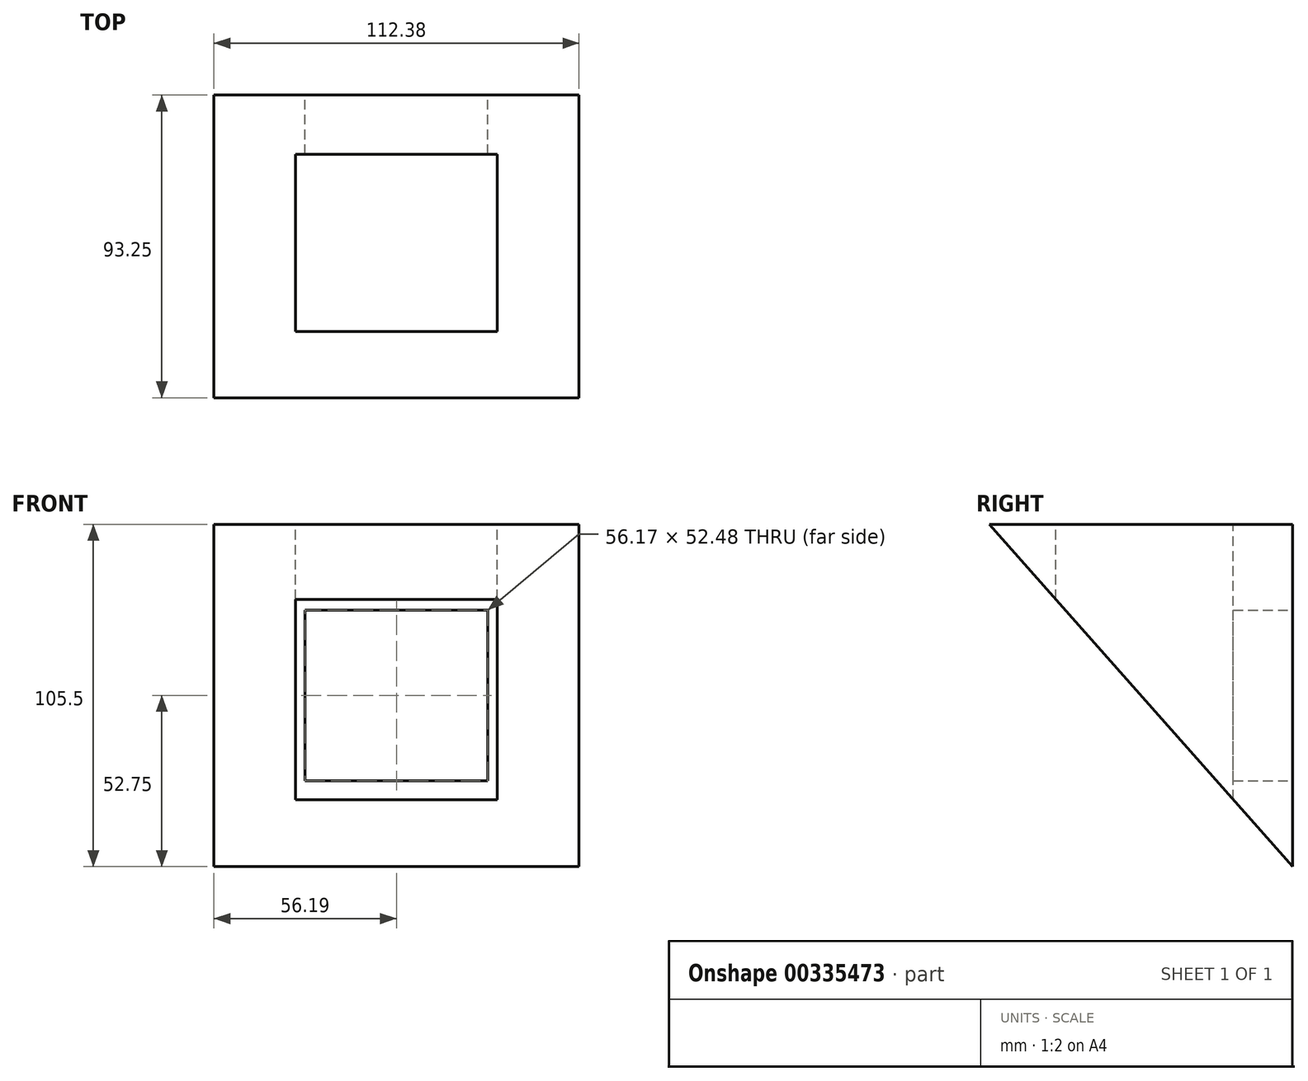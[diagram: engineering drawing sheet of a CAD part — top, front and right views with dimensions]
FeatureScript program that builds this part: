
annotation { "Feature Type Name" : "Feature", "Feature Type Description" : "" }
export const myFeature = defineFeature(function(context is Context, id is Id, definition is map)
    precondition{}
    {
        {
            var Q0;
            Q0=qCreatedBy(makeId("Front.planeOp"),FACE);
            var sketch = newSketch(context, id + "F0", { "sketchPlane" : qUnion([Q0])});
            skLineSegment(sketch, "E0.bottom", {"start": v(28.09, 26.24) * mm, "end": v(-28.09, 26.24) * mm});
            skLineSegment(sketch, "E0.top", {"start": v(28.09, -26.24) * mm, "end": v(-28.09, -26.24) * mm});
            skLineSegment(sketch, "E0.left", {"start": v(28.09, 26.24) * mm, "end": v(28.09, -26.24) * mm});
            skLineSegment(sketch, "E0.right", {"start": v(-28.09, 26.24) * mm, "end": v(-28.09, -26.24) * mm});
            skPoint(sketch, "E0.middle", {"position": v(0, 0) * mm});
            skLineSegment(sketch, "E1.bottom", {"start": v(-56.2, -52.75) * mm, "end": v(56.2, -52.75) * mm});
            skLineSegment(sketch, "E1.top", {"start": v(-56.2, 52.75) * mm, "end": v(56.2, 52.75) * mm});
            skLineSegment(sketch, "E1.left", {"start": v(-56.2, -52.75) * mm, "end": v(-56.2, 52.75) * mm});
            skLineSegment(sketch, "E1.right", {"start": v(56.2, -52.75) * mm, "end": v(56.2, 52.75) * mm});
            skSolve(sketch);
        }
        {
            var Q0;
            Q0=makeQuery(id+"F0.imprint","IMPRINT",FACE,{"disambiguationData":[TD([[makeQuery(id+"F0.imprint","IMPRINT",EDGE,{"derivedFrom":sQuery(id+"F0.wireOp",EDGE,"E0.bottom")}),-1.0]])]});
            extrude(context, id + "F1", {"entities" : qUnion([Q0]), "depth" : 93.25 * mm});
        }
        {
            var Q0;
            Q0=makeQuery(id+"F1.opExtrude","SWEPT_FACE",FACE,{"disambiguationData":[OSD([sQuery(id+"F0.wireOp",EDGE,"E1.left")])]});
            var sketch = newSketch(context, id + "F2", { "sketchPlane" : qUnion([Q0])});
            skLineSegment(sketch, "E2", {"start": v(0, -52.75) * mm, "end": v(93.25, 52.75) * mm});
            skLineSegment(sketch, "E3", {"start": v(93.25, 52.75) * mm, "end": v(93.25, -52.75) * mm});
            skLineSegment(sketch, "E4", {"start": v(93.25, -52.75) * mm, "end": v(0, -52.75) * mm});
            skSolve(sketch);
        }
        {
            var Q0;
            Q0=makeQuery(id+"F2.imprint","IMPRINT",FACE,{"disambiguationData":[TD([[makeQuery(id+"F2.imprint","IMPRINT",EDGE,{"derivedFrom":sQuery(id+"F2.wireOp",EDGE,"E2")}),-1.0]])]});
            extrude(context, id + "F3", {"entities" : qUnion([Q0]), "operationType" : NewBodyOperationType.REMOVE, "endBound" : BoundingType.SYMMETRIC, "depth" : 100000 * mm});
        }
        {
            var Q0;
            Q0=makeQuery(id+"F1.opExtrude","SWEPT_FACE",FACE,{"disambiguationData":[OSD([sQuery(id+"F0.wireOp",EDGE,"E1.top")])]});
            var sketch = newSketch(context, id + "F4", { "sketchPlane" : qUnion([Q0])});
            skLineSegment(sketch, "E5.bottom", {"start": v(31.08, -18.22) * mm, "end": v(-31.08, -18.22) * mm});
            skLineSegment(sketch, "E5.top", {"start": v(31.08, -72.8) * mm, "end": v(-31.08, -72.8) * mm});
            skLineSegment(sketch, "E5.left", {"start": v(31.08, -18.22) * mm, "end": v(31.08, -72.8) * mm});
            skLineSegment(sketch, "E5.right", {"start": v(-31.08, -18.22) * mm, "end": v(-31.08, -72.8) * mm});
            skPoint(sketch, "E5.middle", {"position": v(0, -45.52) * mm});
            skSolve(sketch);
        }
        {
            var Q0;
            Q0=makeQuery(id+"F4.imprint","IMPRINT",FACE,{"disambiguationData":[TD([[makeQuery(id+"F4.imprint","IMPRINT",EDGE,{"derivedFrom":sQuery(id+"F4.wireOp",EDGE,"E5.bottom")}),1.0]])]});
            extrude(context, id + "F5", {"entities" : qUnion([Q0]), "operationType" : NewBodyOperationType.REMOVE, "endBound" : BoundingType.THROUGH_ALL, "oppositeDirection" : true, "depth" : 25 * mm});
        }
        {
            var Q0;
            Q0=qCreatedBy(makeId("Front.planeOp"),FACE);
            cPlane(context, id + "F6", {"entities" : qUnion([Q0]), "cplaneType" : CPlaneType.OFFSET, "offset" : 1 * mm, "width" : 150 * mm, "height" : 150 * mm});
        }
    });
